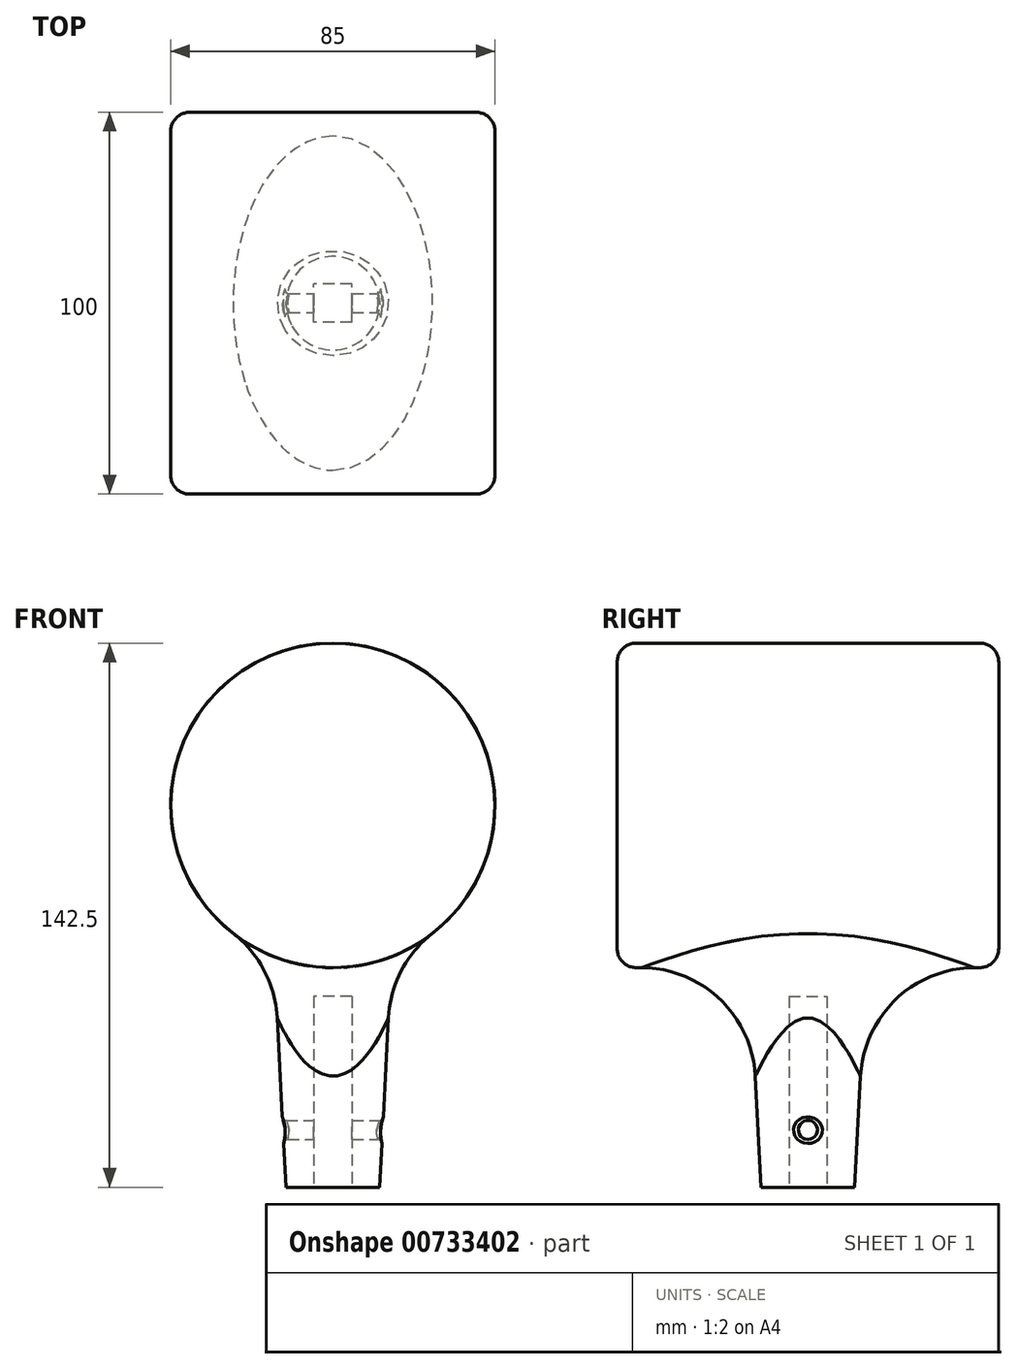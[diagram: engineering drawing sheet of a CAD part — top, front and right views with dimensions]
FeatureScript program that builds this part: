
annotation { "Feature Type Name" : "Feature", "Feature Type Description" : "" }
export const myFeature = defineFeature(function(context is Context, id is Id, definition is map)
    precondition{}
    {
        {
            var Q0;
            Q0=qCreatedBy(makeId("Front.planeOp"),FACE);
            var sketch = newSketch(context, id + "F0", { "sketchPlane" : qUnion([Q0])});
            skCircle(sketch, "E0", {"center": v(0, 0) * mm, "radius": 42.5 * mm});
            skSolve(sketch);
        }
        {
            var Q0;
            Q0=makeQuery(id+"F0.imprint","IMPRINT",FACE,{"disambiguationData":[TD([[makeQuery(id+"F0.imprint","IMPRINT",EDGE,{"derivedFrom":sQuery(id+"F0.wireOp",EDGE,"E0")}),1.0]])]});
            extrude(context, id + "F1", {"entities" : qUnion([Q0]), "endBound" : BoundingType.SYMMETRIC, "depth" : 100 * mm, "offsetDistance" : 25 * mm});
        }
        {
            var Q0;
            Q0=qCreatedBy(makeId("Top.planeOp"),FACE);
            var sketch = newSketch(context, id + "F2", { "sketchPlane" : qUnion([Q0])});
            skCircle(sketch, "E1", {"center": v(0, 0) * mm, "radius": 17.5 * mm});
            skSolve(sketch);
        }
        {
            var Q0;
            Q0=makeQuery(id+"F2.imprint","IMPRINT",FACE,{"disambiguationData":[TD([[makeQuery(id+"F2.imprint","IMPRINT",EDGE,{"derivedFrom":sQuery(id+"F2.wireOp",EDGE,"E1")}),1.0]])]});
            extrude(context, id + "F3", {"entities" : qUnion([Q0]), "operationType" : NewBodyOperationType.ADD, "oppositeDirection" : true, "depth" : 100 * mm, "offsetDistance" : 25 * mm, "hasDraft" : true, "draftAngle" : 3 * degree, "draftPullDirection" : true});
        }
        {
            var Q0;
            Q0=makeQuery(id+"F3.opExtrude","CAP_FACE",FACE,{"disambiguationData":[OSD([sQuery(id+"F2.wireOp",EDGE,"E1")])],"isStart":false});
            var sketch = newSketch(context, id + "F4", { "sketchPlane" : qUnion([Q0])});
            skLineSegment(sketch, "E2.bottom", {"start": v(5, 5) * mm, "end": v(-5, 5) * mm});
            skLineSegment(sketch, "E2.top", {"start": v(5, -5) * mm, "end": v(-5, -5) * mm});
            skLineSegment(sketch, "E2.left", {"start": v(5, 5) * mm, "end": v(5, -5) * mm});
            skLineSegment(sketch, "E2.right", {"start": v(-5, 5) * mm, "end": v(-5, -5) * mm});
            skPoint(sketch, "E2.middle", {"position": v(0, 0) * mm});
            skSolve(sketch);
        }
        {
            var Q0;
            Q0 = qSketchRegion(id + "F4", true);
            extrude(context, id + "F5", {"entities" : qUnion([Q0]), "operationType" : NewBodyOperationType.REMOVE, "oppositeDirection" : true, "depth" : 50 * mm, "offsetDistance" : 25 * mm});
        }
        {
            var Q0;
            Q0=qCreatedBy(makeId("Right.planeOp"),FACE);
            var sketch = newSketch(context, id + "F6", { "sketchPlane" : qUnion([Q0])});
            skCircle(sketch, "E3", {"center": v(0, -85) * mm, "radius": 2.5 * mm});
            skSolve(sketch);
        }
        {
            var Q0;
            Q0 = qSketchRegion(id + "F6", true);
            extrude(context, id + "F7", {"entities" : qUnion([Q0]), "operationType" : NewBodyOperationType.REMOVE, "endBound" : BoundingType.SYMMETRIC, "oppositeDirection" : true, "depth" : 50 * mm, "offsetDistance" : 25 * mm});
        }
        {
            var Q0;
            Q0=makeQuery(id+"F3.boolean.opBoolean","INTERSECT",EDGE,{"derivedFrom":[makeQuery(id+"F1.opExtrude","SWEPT_FACE",FACE,{"disambiguationData":[OSD([sQuery(id+"F0.wireOp",EDGE,"E0")])]}),makeQuery(id+"F3.opExtrude","SWEPT_FACE",FACE,{"disambiguationData":[OSD([sQuery(id+"F2.wireOp",EDGE,"E1")])]})]});
            fillet(context, id + "F8", {"entities" : qUnion([Q0]), "radius" : 30 * mm, "tangentPropagation" : true, "allowEdgeOverflow" : false});
        }
        {
            var Q0;
            Q0=makeQuery(id+"F1.opExtrude","CAP_EDGE",EDGE,{"disambiguationData":[OSD([sQuery(id+"F0.wireOp",EDGE,"E0")])],"isStart":true});
            fillet(context, id + "F9", {"entities" : qUnion([Q0]), "radius" : 5 * mm, "tangentPropagation" : true, "allowEdgeOverflow" : false});
        }
        {
            var Q0;
            Q0=makeQuery(id+"F1.opExtrude","CAP_EDGE",EDGE,{"disambiguationData":[OSD([sQuery(id+"F0.wireOp",EDGE,"E0")])],"isStart":false});
            fillet(context, id + "F10", {"entities" : qUnion([Q0]), "radius" : 5 * mm, "tangentPropagation" : true, "allowEdgeOverflow" : false});
        }
        {
            var Q0;
            Q0=makeQuery(id+"F7.boolean.opBoolean","INTERSECT",EDGE,{"disambiguationData":[OD(1.0)],"derivedFrom":[makeQuery(id+"F3.opExtrude","SWEPT_FACE",FACE,{"disambiguationData":[OSD([sQuery(id+"F2.wireOp",EDGE,"E1")])]}),makeQuery(id+"F7.opExtrude","SWEPT_FACE",FACE,{"disambiguationData":[OSD([sQuery(id+"F6.wireOp",EDGE,"E3")])]})]});
            fillet(context, id + "F11", {"entities" : qUnion([Q0]), "radius" : 1 * mm, "tangentPropagation" : true, "allowEdgeOverflow" : false});
        }
        {
            var Q0;
            Q0=makeQuery(id+"F7.boolean.opBoolean","INTERSECT",EDGE,{"disambiguationData":[OD(0.0)],"derivedFrom":[makeQuery(id+"F3.opExtrude","SWEPT_FACE",FACE,{"disambiguationData":[OSD([sQuery(id+"F2.wireOp",EDGE,"E1")])]}),makeQuery(id+"F7.opExtrude","SWEPT_FACE",FACE,{"disambiguationData":[OSD([sQuery(id+"F6.wireOp",EDGE,"E3")])]})]});
            fillet(context, id + "F12", {"entities" : qUnion([Q0]), "radius" : 1 * mm, "tangentPropagation" : true, "allowEdgeOverflow" : false});
        }
    });
